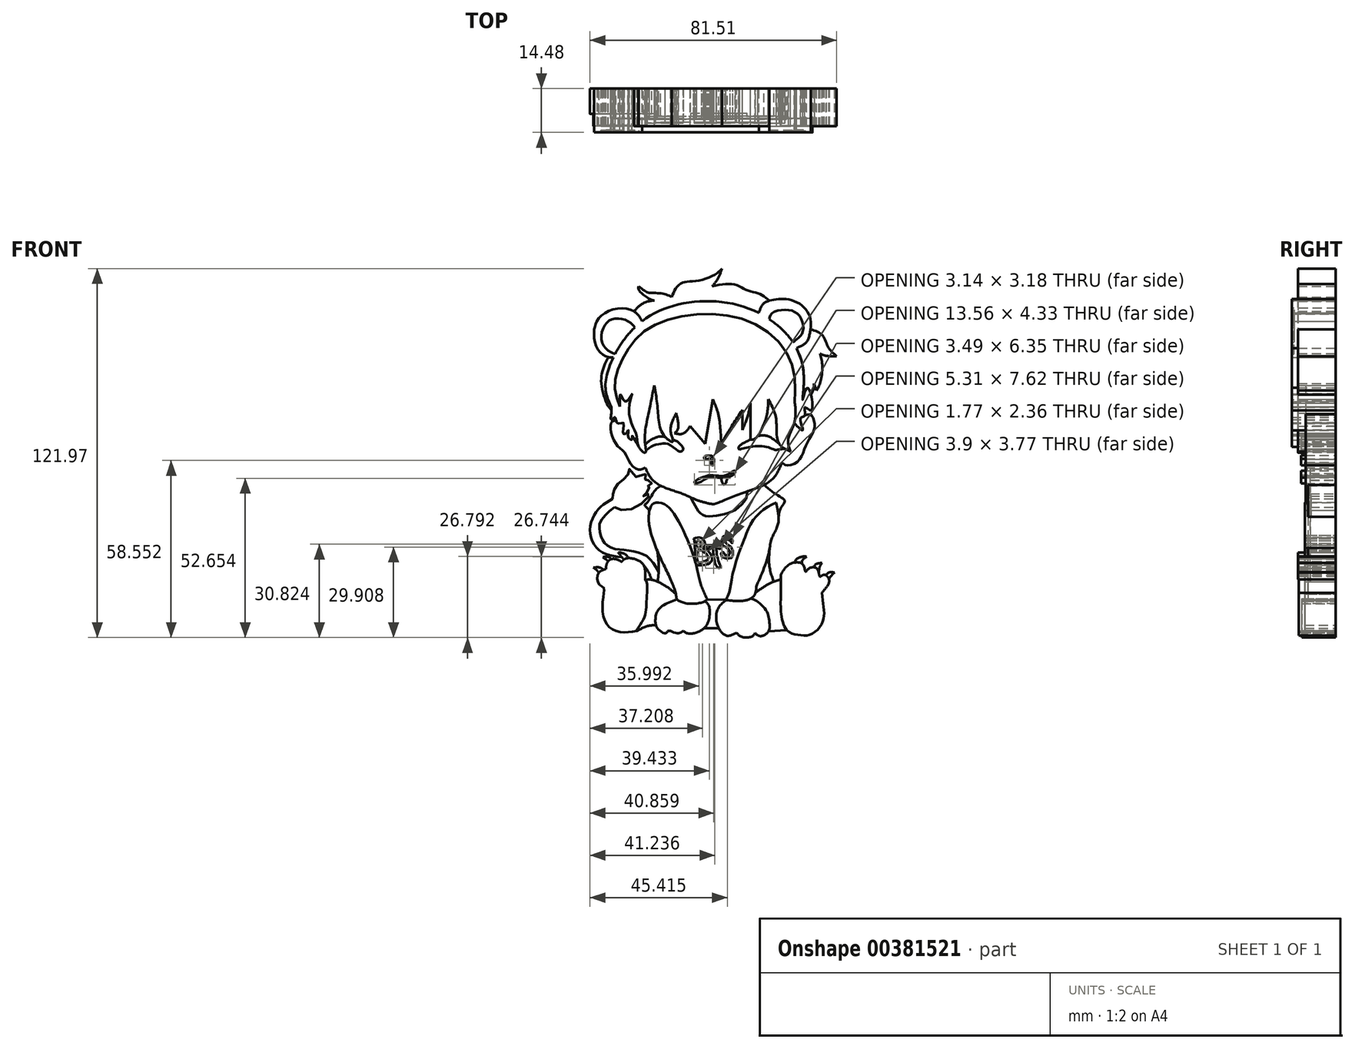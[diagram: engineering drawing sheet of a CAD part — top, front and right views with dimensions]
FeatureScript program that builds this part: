
annotation { "Feature Type Name" : "Feature", "Feature Type Description" : "" }
export const myFeature = defineFeature(function(context is Context, id is Id, definition is map)
    precondition{}
    {
        {
            var Q0;
            Q0=qCreatedBy(makeId("Front.planeOp"),FACE);
            var sketch = newSketch(context, id + "F0", { "sketchPlane" : qUnion([Q0])});
            skFitSpline(sketch, "E0", {"points": [v(-18.55, 26.42) * mm, v(-20.5, 16.98) * mm, v(-21.65, 7.93) * mm, v(-21.53, 4.18) * mm, v(-23.72, 6.12) * mm, v(-24.37, 9.74) * mm, v(-25.8, 13.23) * mm, v(-26.83, 19.7) * mm, v(-25.92, 23.57) * mm, v(-27.99, 21.11) * mm, v(-29.67, 23.31) * mm, v(-29.93, 19.43) * mm], "startDerivative": vector(-14.4, -71.56) * mm, "endDerivative": vector(1.85, -74.93) * mm});
            skFitSpline(sketch, "E1", {"points": [v(-18.55, 26.42) * mm, v(-17.39, 18.27) * mm, v(-15.7, 10.38) * mm, v(-12.48, 7.8) * mm, v(-13.12, 11.29) * mm, v(-11.31, 17.24) * mm], "startDerivative": vector(5.92, -33.92) * mm, "endDerivative": vector(14.7, 28.25) * mm});
            skFitSpline(sketch, "E2", {"points": [v(-11.83, 10.64) * mm, v(-10.67, 12.2) * mm, v(-11.31, 17.24) * mm], "startDerivative": vector(3.83, 3.28) * mm, "endDerivative": vector(-2.31, 9.42) * mm});
            skFitSpline(sketch, "E3", {"points": [v(-11.83, 10.64) * mm, v(-8.73, 10.64) * mm, v(-5.24, 16.98) * mm, v(-5.5, 23.18) * mm], "startDerivative": vector(12.38, -3.46) * mm, "endDerivative": vector(-3, 16.24) * mm});
            skFitSpline(sketch, "E4", {"points": [v(-6.7, 13) * mm, v(-1.74, 7.07) * mm], "startDerivative": vector(4.96, -5.94) * mm, "endDerivative": vector(4.96, -5.94) * mm});
            skFitSpline(sketch, "E5", {"points": [v(0.8, 21.84) * mm, v(-1.74, 7.07) * mm], "startDerivative": vector(-2.54, -14.77) * mm, "endDerivative": vector(-2.54, -14.77) * mm});
            skFitSpline(sketch, "E6", {"points": [v(0.8, 21.84) * mm, v(2.73, 16.3) * mm, v(3.57, 7.07) * mm], "startDerivative": vector(4.99, -11.59) * mm, "endDerivative": vector(0.71, -17.72) * mm});
            skFitSpline(sketch, "E7", {"points": [v(10.53, 18.24) * mm, v(5.58, 10.6) * mm, v(3.57, 7.07) * mm], "startDerivative": vector(-9.23, -13.9) * mm, "endDerivative": vector(-4.37, -8.05) * mm});
            skFitSpline(sketch, "E8", {"points": [v(10.53, 18.24) * mm, v(10.53, 11.7) * mm], "startDerivative": vector(0, -6.54) * mm, "endDerivative": vector(0, -6.54) * mm});
            skFitSpline(sketch, "E9", {"points": [v(13.21, 20.58) * mm, v(12.37, 16.4) * mm, v(10.53, 11.7) * mm], "startDerivative": vector(-1.32, -8.68) * mm, "endDerivative": vector(-4, -9.09) * mm});
            skFitSpline(sketch, "E10", {"points": [v(13.21, 20.58) * mm, v(13.21, 8.51) * mm], "startDerivative": vector(0, -12.07) * mm, "endDerivative": vector(0, -12.07) * mm});
            skFitSpline(sketch, "E11", {"points": [v(19.08, 21.84) * mm, v(18.4, 15.64) * mm, v(14.8, 8.85) * mm, v(13.21, 8.51) * mm], "startDerivative": vector(0.03, -15.04) * mm, "endDerivative": vector(-7.8, 0.75) * mm});
            skFitSpline(sketch, "E12", {"points": [v(19.08, 21.84) * mm, v(21.5, 16.56) * mm, v(21.85, 11.7) * mm, v(22.77, 7.07) * mm, v(26.46, 4.57) * mm], "startDerivative": vector(11.06, -19.58) * mm, "endDerivative": vector(18.37, -8.35) * mm});
            skFitSpline(sketch, "E13", {"points": [v(24.28, 31.23) * mm, v(27.46, 22.85) * mm, v(27.71, 13.96) * mm, v(25.7, 8.51) * mm, v(26.46, 4.57) * mm], "startDerivative": vector(12.77, -28.04) * mm, "endDerivative": vector(7.38, -20.16) * mm});
            skFitSpline(sketch, "E14", {"points": [v(-29.93, 19.43) * mm, v(-31.64, 26.54) * mm, v(-28.7, 35.92) * mm, v(-20.76, 45.07) * mm, v(-4.33, 49.9) * mm, v(14.79, 46.68) * mm, v(26.46, 34.71) * mm, v(27.9, 20.58) * mm], "startDerivative": vector(-24.7, 65.1) * mm, "endDerivative": vector(-3.9, -98.8) * mm});
            skFitSpline(sketch, "E15", {"points": [v(-32.73, 19.2) * mm, v(-34.7, 26.32) * mm, v(-30.8, 38.1) * mm, v(-21.48, 48.47) * mm, v(-7.19, 53.83) * mm, v(10.53, 52.58) * mm, v(24.97, 43.64) * mm, v(30.87, 29.71) * mm, v(30.5, 21.71) * mm, v(32.12, 25.6) * mm, v(33.37, 18.27) * mm, v(31.22, 19.2) * mm, v(31.22, 16.49) * mm, v(29.8, 15.6) * mm, v(30.5, 11.7) * mm, v(27.71, 13.96) * mm], "startDerivative": vector(-45.63, 102.3) * mm, "endDerivative": vector(-89.01, 91.48) * mm});
            skFitSpline(sketch, "E16", {"points": [v(-32.73, 19.2) * mm, v(-32.73, 17.51) * mm, v(-32.73, 15.07) * mm, v(-31.52, 15.86) * mm, v(-30.8, 13.96) * mm, v(-28.74, 13.96) * mm, v(-28.83, 10.55) * mm, v(-27.87, 10.55) * mm, v(-27.09, 11.7) * mm, v(-27.09, 9.24) * mm, v(-25.92, 8.51) * mm, v(-25.92, 9.77) * mm, v(-23.72, 6.12) * mm], "startDerivative": vector(1.52, -17.26) * mm, "endDerivative": vector(25.91, -48.27) * mm});
            skFitSpline(sketch, "E17", {"points": [v(-33.7, 35.78) * mm, v(-35.74, 31) * mm, v(-35.8, 25.32) * mm, v(-33.7, 19.43) * mm, v(-32.69, 18.31) * mm], "startDerivative": vector(-8.88, -17.25) * mm, "endDerivative": vector(6.63, -5.51) * mm});
            skFitSpline(sketch, "E18", {"points": [v(-32.11, 35.62) * mm, v(-33.7, 35.78) * mm, v(-36.86, 37.78) * mm, v(-38.46, 42.85) * mm, v(-38.26, 45.49) * mm, v(-36.8, 48.78) * mm, v(-30.8, 51.81) * mm, v(-24.86, 50.62) * mm, v(-22.6, 47.65) * mm], "startDerivative": vector(-18.4, 0.14) * mm, "endDerivative": vector(14.36, -27.23) * mm});
            skFitSpline(sketch, "E19", {"points": [v(-31.5, 36.82) * mm, v(-33.7, 37.9) * mm, v(-35.98, 41.05) * mm, v(-35.2, 45.75) * mm, v(-32.73, 48.24) * mm, v(-28.6, 48.24) * mm, v(-25.92, 46.76) * mm, v(-25.03, 45.56) * mm], "startDerivative": vector(-17.52, 6.5) * mm, "endDerivative": vector(7.45, -12.42) * mm});
            skFitSpline(sketch, "E20", {"points": [v(-15.84, 53.96) * mm, v(-19.35, 54.42) * mm, v(-22.95, 53.12) * mm, v(-25.25, 50.87) * mm], "startDerivative": vector(-10.34, 2.5) * mm, "endDerivative": vector(-6.42, -7.57) * mm});
            skFitSpline(sketch, "E21", {"points": [v(-12.74, 55.63) * mm, v(-15.75, 56.76) * mm, v(-19.48, 56.97) * mm, v(-20.9, 57.22) * mm, v(-23.72, 59.15) * mm], "startDerivative": vector(-10.48, 5.16) * mm, "endDerivative": vector(-11.44, 8.74) * mm});
            skFitSpline(sketch, "E22", {"points": [v(-18.55, 54.43) * mm, v(-20.44, 55.21) * mm, v(-23.72, 58.1) * mm, v(-23.72, 59.15) * mm], "startDerivative": vector(-5.2, 1.51) * mm, "endDerivative": vector(1.36, 4.15) * mm});
            skFitSpline(sketch, "E23", {"points": [v(-12.74, 55.63) * mm, v(-11.44, 58.43) * mm, v(-9.02, 60.44) * mm, v(-5.13, 60.9) * mm, v(1.2, 62.89) * mm, v(3.8, 65.04) * mm], "startDerivative": vector(6, 16.35) * mm, "endDerivative": vector(11.38, 12.05) * mm});
            skFitSpline(sketch, "E24", {"points": [v(0.6, 59.21) * mm, v(2.46, 61.66) * mm, v(3.8, 65.04) * mm], "startDerivative": vector(4.2, 4.78) * mm, "endDerivative": vector(2.23, 6.85) * mm});
            skFitSpline(sketch, "E25", {"points": [v(0.6, 59.21) * mm, v(7.96, 59.8) * mm, v(12.2, 57.9) * mm, v(16.43, 56.62) * mm, v(19.45, 54.42) * mm], "startDerivative": vector(26.23, 5.07) * mm, "endDerivative": vector(12.76, -11.67) * mm});
            skFitSpline(sketch, "E26", {"points": [v(19.45, 54.42) * mm, v(17.44, 53.37) * mm, v(16, 50.35) * mm], "startDerivative": vector(-4.85, -1.6) * mm, "endDerivative": vector(-2.17, -6.41) * mm});
            skFitSpline(sketch, "E27", {"points": [v(19.45, 54.42) * mm, v(23.82, 55.04) * mm, v(29.49, 53.41) * mm, v(32.98, 48.8) * mm, v(32.92, 43.94) * mm, v(31.6, 40.57) * mm, v(28.44, 38.77) * mm], "startDerivative": vector(25.67, 5.92) * mm, "endDerivative": vector(-24.61, -9.76) * mm});
            skFitSpline(sketch, "E28", {"points": [v(19.45, 48.33) * mm, v(20.32, 50.23) * mm, v(25.25, 51.42) * mm, v(29.3, 49.55) * mm, v(30.74, 45.18) * mm, v(29.3, 42.25) * mm, v(27.21, 40.81) * mm], "startDerivative": vector(3.02, 16.1) * mm, "endDerivative": vector(-15.56, -8.68) * mm});
            skFitSpline(sketch, "E29", {"points": [v(33.09, 44.93) * mm, v(36.97, 43.06) * mm, v(38.97, 39.01) * mm, v(41.7, 36.08) * mm], "startDerivative": vector(13.33, -3.73) * mm, "endDerivative": vector(9.57, -7.95) * mm});
            skFitSpline(sketch, "E30", {"points": [v(36.29, 36.95) * mm, v(37.97, 36.27) * mm, v(41.7, 36.08) * mm], "startDerivative": vector(3.64, -1.95) * mm, "endDerivative": vector(7, 0.08) * mm});
            skFitSpline(sketch, "E31", {"points": [v(36.29, 36.95) * mm, v(36.97, 32.9) * mm, v(36.29, 27.3) * mm, v(35.16, 24.8) * mm], "startDerivative": vector(2.82, -11.18) * mm, "endDerivative": vector(-4.41, -7.86) * mm});
            skFitSpline(sketch, "E32", {"points": [v(34.23, 27.1) * mm, v(35.16, 24.8) * mm], "startDerivative": vector(0.94, -2.3) * mm, "endDerivative": vector(0.94, -2.3) * mm});
            skFitSpline(sketch, "E33", {"points": [v(34.23, 27.1) * mm, v(34.04, 25) * mm, v(33.25, 23.33) * mm], "startDerivative": vector(-0.03, -4.23) * mm, "endDerivative": vector(-1.96, -3.32) * mm});
            skFitSpline(sketch, "E34", {"points": [v(-21.53, -0.78) * mm, v(-23.65, -1.43) * mm, v(-26.44, 0.62) * mm, v(-28.34, 4.18) * mm, v(-30.99, 6.79) * mm, v(-32.97, 11.7) * mm, v(-32.6, 14.35) * mm, v(-31.2, 14.93) * mm], "startDerivative": vector(-16.97, -9.49) * mm, "endDerivative": vector(16.15, 3.19) * mm});
            skFitSpline(sketch, "E35", {"points": [v(-22.2, 0.3) * mm, v(-21.53, -0.78) * mm, v(-18.65, -5.3) * mm, v(-9.77, -9.2) * mm, v(-4.64, -11.42) * mm, v(0, -12.73) * mm], "startDerivative": vector(6.28, -8.26) * mm, "endDerivative": vector(24.05, -5.75) * mm});
            skFitSpline(sketch, "E36", {"points": [v(0, -12.73) * mm, v(1.5, -12.73) * mm, v(5.45, -11.11) * mm, v(13.44, -8.2) * mm, v(20.57, -4.5) * mm, v(23.66, 0.97) * mm], "startDerivative": vector(13, -1.7) * mm, "endDerivative": vector(11.23, 27.55) * mm});
            skFitSpline(sketch, "E37", {"points": [v(23.66, 0.97) * mm, v(25, 0) * mm, v(28.48, 0.97) * mm, v(30.62, 4.18) * mm, v(32.6, 8.64) * mm, v(34.23, 11.65) * mm, v(34.23, 14.91) * mm, v(33.12, 16.8) * mm, v(31.22, 16.49) * mm], "startDerivative": vector(12.26, -13.1) * mm, "endDerivative": vector(-20.68, -7.96) * mm});
            skFitSpline(sketch, "E38", {"points": [v(9.66, 5.22) * mm, v(13.27, 6.12) * mm, v(18.51, 6.12) * mm, v(21.73, 5.1) * mm, v(23.66, 5.3) * mm], "startDerivative": vector(12.97, 4) * mm, "endDerivative": vector(12.7, -2.3) * mm});
            skFitSpline(sketch, "E39", {"points": [v(9.66, 5.22) * mm, v(9.28, 5.6) * mm, v(9.66, 6.43) * mm, v(13.21, 8.51) * mm], "startDerivative": vector(-2.54, 1.7) * mm, "endDerivative": vector(7.96, 3.9) * mm});
            skFitSpline(sketch, "E40", {"points": [v(15.65, 9.74) * mm, v(18.76, 9.74) * mm, v(22.77, 7.07) * mm], "startDerivative": vector(6.92, 1.07) * mm, "endDerivative": vector(7.3, -6.15) * mm});
            skFitSpline(sketch, "E41", {"points": [v(-20.97, 5.22) * mm, v(-18.5, 6.63) * mm, v(-16.24, 7.07) * mm, v(-13.94, 7.07) * mm, v(-10.74, 4.78) * mm, v(-9.76, 4.57) * mm, v(-9.01, 5.22) * mm, v(-9.98, 7.07) * mm, v(-12.5, 8.7) * mm], "startDerivative": vector(16.81, 12.03) * mm, "endDerivative": vector(-18.51, 9.4) * mm});
            skFitSpline(sketch, "E42", {"points": [v(-14.96, 9.41) * mm, v(-16.17, 9.54) * mm, v(-17.82, 9.3) * mm, v(-20.17, 8.1) * mm, v(-21.54, 6.84) * mm], "startDerivative": vector(-5.79, 0.89) * mm, "endDerivative": vector(-4.67, -5.03) * mm});
            skFitSpline(sketch, "E43", {"points": [v(-1.94, 2.81) * mm, v(0.8, 2.81) * mm, v(0.8, 0) * mm, v(0.3, 0.5) * mm, v(0.4, 1.58) * mm, v(0.28, 2.07) * mm, v(-0.32, 2.16) * mm, v(-1.16, 2.06) * mm, v(-1.74, 2.13) * mm, v(-2.04, 2.2) * mm, v(-1.94, 2.81) * mm]});
            skFitSpline(sketch, "E44", {"points": [v(-5.38, -5.64) * mm, v(-2.06, -3.76) * mm, v(0.94, -3.32) * mm, v(4.95, -3.34) * mm, v(7.63, -1.9) * mm, v(8.1, -1.83) * mm, v(8.12, -2.54) * mm, v(5.68, -3.9) * mm, v(3.31, -4.03) * mm, v(0.65, -4.08) * mm, v(-1.5, -4.42) * mm, v(-4.23, -5.88) * mm, v(-5.38, -5.64) * mm]});
            skFitSpline(sketch, "E45", {"points": [v(3.6, -4.04) * mm, v(3.8, -5.37) * mm, v(4.53, -6.45) * mm, v(5.36, -5.05) * mm, v(5.68, -3.9) * mm], "startDerivative": vector(0.23, -4.92) * mm, "endDerivative": vector(0.97, 4.2) * mm});
            skFitSpline(sketch, "E46", {"points": [v(-20.17, -14.87) * mm, v(-18.97, -12.73) * mm, v(-15.35, -12.73) * mm, v(-10.13, -19.2) * mm, v(-4.86, -32.28) * mm, v(-3.11, -39.48) * mm, v(-1, -44.31) * mm], "startDerivative": vector(7.43, 24.09) * mm, "endDerivative": vector(15.57, -30.67) * mm});
            skFitSpline(sketch, "E47", {"points": [v(-1, -44.31) * mm, v(-2.82, -45.35) * mm, v(-8.44, -45.54) * mm, v(-11.15, -44.31) * mm], "startDerivative": vector(-5.43, -4.42) * mm, "endDerivative": vector(-7.24, 4.73) * mm});
            skFitSpline(sketch, "E48", {"points": [v(-1.84, -44.93) * mm, v(-0.5, -46.53) * mm, v(-1, -52.33) * mm, v(-4.2, -55.13) * mm, v(-7.64, -55.53) * mm, v(-9.4, -54.13) * mm], "startDerivative": vector(10.15, -7.4) * mm, "endDerivative": vector(-9.3, 10.8) * mm});
            skFitSpline(sketch, "E49", {"points": [v(-8.9, -54.71) * mm, v(-11.14, -55.53) * mm, v(-13.94, -54.71) * mm, v(-14.7, -55.53) * mm, v(-17.4, -54.03) * mm, v(-18.2, -51.23) * mm, v(-17.04, -47.53) * mm, v(-11.15, -44.31) * mm], "startDerivative": vector(-16.16, -11.36) * mm, "endDerivative": vector(33.64, 12.73) * mm});
            skFitSpline(sketch, "E50", {"points": [v(-11.15, -44.31) * mm, v(-12, -40.47) * mm, v(-15.9, -31.94) * mm, v(-20.17, -20.22) * mm, v(-20.17, -14.87) * mm], "startDerivative": vector(-2.92, 19.6) * mm, "endDerivative": vector(2.63, 22.62) * mm});
            skFitSpline(sketch, "E51", {"points": [v(-17.5, -28.36) * mm, v(-17.07, -33.89) * mm, v(-17.43, -38.45) * mm], "startDerivative": vector(1.25, -10.8) * mm, "endDerivative": vector(-1.14, -9.35) * mm});
            skFitSpline(sketch, "E52", {"points": [v(-17.43, -38.45) * mm, v(-13.94, -40.47) * mm, v(-11.45, -42.53) * mm], "startDerivative": vector(6.95, -3.7) * mm, "endDerivative": vector(4.98, -4.46) * mm});
            skFitSpline(sketch, "E53", {"points": [v(-17.43, -38.45) * mm, v(-19.45, -37.83) * mm, v(-20.72, -37.78) * mm], "startDerivative": vector(-3.78, 1.39) * mm, "endDerivative": vector(-2.77, -0.12) * mm});
            skFitSpline(sketch, "E54", {"points": [v(-18.03, -52.85) * mm, v(-21.87, -53.5) * mm, v(-24.37, -54.71) * mm, v(-22.2, -50.99) * mm, v(-21.1, -44.8) * mm, v(-21.15, -38.45) * mm, v(-21.53, -37.91) * mm, v(-20.72, -37.78) * mm], "startDerivative": vector(-23.55, -0.55) * mm, "endDerivative": vector(15.9, 0.86) * mm});
            skFitSpline(sketch, "E55", {"points": [v(-21.53, -37.91) * mm, v(-21.53, -35.7) * mm, v(-22.2, -32.77) * mm, v(-24.92, -31.03) * mm, v(-27.81, -30.78) * mm, v(-29.3, -31.92) * mm, v(-29.72, -33.4) * mm], "startDerivative": vector(0.27, 13.05) * mm, "endDerivative": vector(-1.76, -11.54) * mm});
            skFitSpline(sketch, "E56", {"points": [v(-29.3, -31.92) * mm, v(-30.66, -31.2) * mm, v(-33.16, -31.16) * mm, v(-34.48, -33.58) * mm, v(-34.05, -35.53) * mm], "startDerivative": vector(-5.6, 3.66) * mm, "endDerivative": vector(3, -7.5) * mm});
            skFitSpline(sketch, "E57", {"points": [v(-34.45, -34.25) * mm, v(-36.22, -34.93) * mm, v(-37.24, -36.13) * mm, v(-36.86, -39.27) * mm, v(-35.29, -40.46) * mm, v(-35.29, -42.75) * mm, v(-35.54, -49.16) * mm, v(-33.42, -53.5) * mm, v(-29.3, -55.15) * mm, v(-24.37, -54.71) * mm], "startDerivative": vector(-22.52, -7.15) * mm, "endDerivative": vector(36.62, 6.5) * mm});
            skFitSpline(sketch, "E58", {"points": [v(-36.95, -35.53) * mm, v(-37.43, -34.79) * mm, v(-38.65, -33.79) * mm], "startDerivative": vector(-0.9, 1.74) * mm, "endDerivative": vector(-2.44, 1.75) * mm});
            skFitSpline(sketch, "E59", {"points": [v(-35.46, -34.6) * mm, v(-36.33, -33.86) * mm, v(-38.65, -33.79) * mm], "startDerivative": vector(-1.74, 2.13) * mm, "endDerivative": vector(-4.5, -0.37) * mm});
            skFitSpline(sketch, "E60", {"points": [v(-32.82, -31.01) * mm, v(-33.23, -30.52) * mm, v(-34.48, -30.2) * mm, v(-35.54, -30.34) * mm], "startDerivative": vector(-1.12, 1.97) * mm, "endDerivative": vector(-2.84, -0.68) * mm});
            skFitSpline(sketch, "E61", {"points": [v(-33.84, -31.79) * mm, v(-34.3, -31.26) * mm, v(-35.12, -30.73) * mm, v(-35.54, -30.34) * mm], "startDerivative": vector(-1.17, 1.7) * mm, "endDerivative": vector(-1.2, 1.35) * mm});
            skFitSpline(sketch, "E62", {"points": [v(-27.11, -30.67) * mm, v(-28.11, -29.42) * mm, v(-30, -28.83) * mm, v(-30.46, -28.86) * mm], "startDerivative": vector(-1.98, 3.63) * mm, "endDerivative": vector(-1.77, -0.37) * mm});
            skFitSpline(sketch, "E63", {"points": [v(-28.6, -31.16) * mm, v(-29.3, -30.34) * mm, v(-30.46, -28.86) * mm], "startDerivative": vector(-1.53, 1.76) * mm, "endDerivative": vector(-2.17, 2.79) * mm});
            skFitSpline(sketch, "E64", {"points": [v(-17.1, -35.2) * mm, v(-20.17, -30.78) * mm, v(-23.72, -28.86) * mm, v(-28.45, -27.99) * mm, v(-32.49, -27.36) * mm, v(-35.2, -25.35) * mm, v(-36.41, -22.56) * mm, v(-36.41, -18.76) * mm, v(-31.67, -13.8) * mm], "startDerivative": vector(-20.27, 35.87) * mm, "endDerivative": vector(38.72, 30.91) * mm});
            skFitSpline(sketch, "E65", {"points": [v(-19.45, -37.83) * mm, v(-20.32, -35.53) * mm, v(-22.2, -32.77) * mm], "startDerivative": vector(-1.52, 4.93) * mm, "endDerivative": vector(-3.93, 5.17) * mm});
            skFitSpline(sketch, "E66", {"points": [v(-32.4, -11.11) * mm, v(-36.52, -13.94) * mm, v(-39.35, -18.62) * mm, v(-39.35, -24.34) * mm, v(-35.54, -28.86) * mm, v(-29.3, -30.34) * mm], "startDerivative": vector(-23.27, -13.18) * mm, "endDerivative": vector(31.19, -3.31) * mm});
            skFitSpline(sketch, "E67", {"points": [v(-26.65, -1.16) * mm, v(-27.15, -2.86) * mm, v(-30.46, -6) * mm, v(-32.1, -8.8) * mm, v(-32.4, -11.11) * mm, v(-31.67, -13.8) * mm, v(-24.37, -13.8) * mm, v(-20.32, -9.47) * mm, v(-22.2, -10.21) * mm, v(-20.17, -7.82) * mm, v(-20.72, -6.82) * mm, v(-19.45, -6.16) * mm, v(-20.72, -4.92) * mm, v(-21.53, -4.76) * mm, v(-21.53, -2.7) * mm, v(-24.37, -3.9) * mm, v(-26.65, -1.16) * mm]});
            skFitSpline(sketch, "E68", {"points": [v(-6.49, -10.62) * mm, v(-4.75, -13.8) * mm, v(-2.44, -16.5) * mm, v(2.19, -16.57) * mm, v(7.97, -14.87) * mm, v(11.69, -11.11) * mm, v(12.16, -8.65) * mm], "startDerivative": vector(10.75, -20.38) * mm, "endDerivative": vector(0.6, 18.24) * mm});
            skFitSpline(sketch, "E69", {"points": [v(21.73, -12.3) * mm, v(22.36, -15.55) * mm, v(22.36, -19.43) * mm, v(20.07, -24.75) * mm, v(19.43, -28.5) * mm, v(16.07, -38) * mm, v(15.25, -39.94) * mm, v(14.64, -42.79) * mm, v(11.29, -44.72) * mm, v(5.18, -44.52) * mm], "startDerivative": vector(7.06, -33.3) * mm, "endDerivative": vector(-48.82, 6.12) * mm});
            skFitSpline(sketch, "E70", {"points": [v(21.73, -12.3) * mm, v(17.24, -14.93) * mm, v(13.5, -19.18) * mm, v(11.41, -23.78) * mm, v(10.62, -25.82) * mm, v(7.41, -35.62) * mm, v(6.55, -40.8) * mm, v(5.18, -44.52) * mm], "startDerivative": vector(-32.36, -16.31) * mm, "endDerivative": vector(-12.87, -29.45) * mm});
            skFitSpline(sketch, "E71", {"points": [v(14.94, -42.03) * mm, v(20, -38.85) * mm, v(23.17, -37.77) * mm], "startDerivative": vector(9.3, 6.4) * mm, "endDerivative": vector(7.09, 1.88) * mm});
            skFitSpline(sketch, "E72", {"points": [v(19.86, -25.58) * mm, v(19.69, -26.86) * mm, v(19.43, -32.74) * mm, v(20.97, -38.44) * mm], "startDerivative": vector(-0.8, -5.34) * mm, "endDerivative": vector(4.98, -13.2) * mm});
            skFitSpline(sketch, "E73", {"points": [v(5.18, -44.52) * mm, v(2.37, -47.7) * mm, v(2.37, -52.88) * mm, v(5.18, -56.27) * mm, v(8.7, -55.4) * mm], "startDerivative": vector(-13.55, -11.26) * mm, "endDerivative": vector(15.98, 7.7) * mm});
            skFitSpline(sketch, "E74", {"points": [v(8.7, -55.4) * mm, v(10.5, -56.77) * mm, v(13.92, -56.48) * mm, v(14.75, -55.4) * mm], "startDerivative": vector(4.3, -5.03) * mm, "endDerivative": vector(1.97, 4.63) * mm});
            skFitSpline(sketch, "E75", {"points": [v(14.75, -55.4) * mm, v(16.55, -56.48) * mm, v(19.21, -54.83) * mm, v(19.43, -51.37) * mm, v(18.42, -47.92) * mm, v(14.75, -44.52) * mm, v(13.26, -44.07) * mm], "startDerivative": vector(11.47, -11.44) * mm, "endDerivative": vector(-10.98, 1.57) * mm});
            skFitSpline(sketch, "E76", {"points": [v(-5.56, -24.26) * mm, v(-5.35, -24.71) * mm, v(-5.1, -27.38) * mm, v(-4.86, -32.28) * mm], "startDerivative": vector(1.47, -2.28) * mm, "endDerivative": vector(0.52, -10.42) * mm});
            skFitSpline(sketch, "E77", {"points": [v(-5.56, -24.26) * mm, v(-3.9, -23.84) * mm, v(-2.2, -24.62) * mm, v(-1.9, -26.77) * mm, v(-2.38, -27.5) * mm, v(-1.08, -28.04) * mm, v(0.58, -30.46) * mm, v(0.31, -31.73) * mm, v(-1.38, -32.85) * mm, v(-4.65, -33.06) * mm], "startDerivative": vector(15.22, 6) * mm, "endDerivative": vector(-23.92, 0.84) * mm});
            skFitSpline(sketch, "E78", {"points": [v(-4.4, -24.92) * mm, v(-4.32, -27.16) * mm, v(-3.23, -26.86) * mm, v(-3.02, -25.65) * mm, v(-4.4, -24.92) * mm]});
            skFitSpline(sketch, "E79", {"points": [v(-4.04, -28.25) * mm, v(-4.01, -31.97) * mm, v(-2.32, -31.8) * mm, v(-0.72, -30.98) * mm, v(-1.23, -29.37) * mm, v(-4.04, -28.25) * mm]});
            skFitSpline(sketch, "E80", {"points": [v(-1.5, -26.44) * mm, v(1.46, -26.38) * mm, v(3.3, -26.38) * mm], "startDerivative": vector(5.62, 0.14) * mm, "endDerivative": vector(3.94, -0.02) * mm});
            skFitSpline(sketch, "E81", {"points": [v(-1.5, -26.44) * mm, v(-1.5, -27.22) * mm, v(0.98, -27.2) * mm], "startDerivative": vector(-0.7, -2.59) * mm, "endDerivative": vector(5.12, 0.76) * mm});
            skFitSpline(sketch, "E82", {"points": [v(3.3, -26.38) * mm, v(3.73, -26.95) * mm, v(3.3, -27.56) * mm, v(1.95, -27.2) * mm], "startDerivative": vector(2.1, -1.79) * mm, "endDerivative": vector(-3.67, 1.78) * mm});
            skFitSpline(sketch, "E83", {"points": [v(0.98, -27.2) * mm, v(0.98, -28.7) * mm, v(1.28, -31.19) * mm, v(1.98, -33.27) * mm, v(2.94, -34) * mm, v(3.3, -33.55) * mm, v(2.82, -31.97) * mm, v(2.16, -29.67) * mm, v(1.95, -27.2) * mm], "startDerivative": vector(-0.39, -12.11) * mm, "endDerivative": vector(-0.73, 16.74) * mm});
            skFitSpline(sketch, "E84", {"points": [v(4.88, -29.58) * mm, v(4.34, -28.8) * mm, v(3.76, -28.65) * mm, v(3.49, -29.43) * mm, v(4.58, -30.73) * mm, v(6.4, -30.8) * mm, v(7.24, -30.34) * mm, v(7.42, -29.52) * mm, v(7.24, -27.5) * mm, v(6.09, -26.44) * mm, v(4.9, -25.53) * mm, v(4.88, -24.74) * mm, v(5.58, -24.14) * mm, v(6.63, -25.08) * mm, v(7.2, -25.74) * mm, v(7.45, -25.1) * mm, v(6.82, -23.84) * mm, v(6.12, -23.23) * mm, v(4.6, -23.23) * mm, v(3.88, -24.53) * mm, v(4, -26.38) * mm, v(5.94, -27.56) * mm, v(6.48, -29.22) * mm, v(6, -29.83) * mm, v(4.88, -29.58) * mm]});
            skFitSpline(sketch, "E85", {"points": [v(-20.17, -14.87) * mm, v(-21.7, -13.09) * mm, v(-21.03, -12.48) * mm, v(-18.54, -8.6) * mm, v(-16.41, -6.75) * mm], "startDerivative": vector(-9.52, 8.87) * mm, "endDerivative": vector(8.07, 5.28) * mm});
            skFitSpline(sketch, "E86", {"points": [v(17.65, -6.49) * mm, v(22.83, -10.29) * mm, v(24.56, -11.76) * mm, v(23.18, -14.3) * mm, v(22.56, -17.06) * mm], "startDerivative": vector(16.09, -12.71) * mm, "endDerivative": vector(-0.92, -12.1) * mm});
            skLineSegment(sketch, "E87", {"start": v(-1, -44.31) * mm, "end": v(5.18, -44.52) * mm});
            skLineSegment(sketch, "E88", {"start": v(-2.05, -53.82) * mm, "end": v(0, -53.82) * mm});
            skLineSegment(sketch, "E89", {"start": v(0, -53.82) * mm, "end": v(2.76, -53.82) * mm});
            skLineSegment(sketch, "E90", {"start": v(19.21, -54.83) * mm, "end": v(25.25, -54.47) * mm});
            skLineSegment(sketch, "E91", {"start": v(23.17, -37.77) * mm, "end": v(23.3, -37.77) * mm});
            skLineSegment(sketch, "E92", {"start": v(-8.9, -54.71) * mm, "end": v(-8.87, -54.71) * mm});
            skFitSpline(sketch, "E93", {"points": [v(23.3, -37.77) * mm, v(23.3, -36.4) * mm, v(24.32, -34.46) * mm, v(26.76, -32.42) * mm, v(30.63, -32.83) * mm, v(31.44, -35.17) * mm, v(32.36, -34.25) * mm, v(35.2, -34.15) * mm, v(36.22, -36.8) * mm, v(37.44, -36.19) * mm, v(39.27, -38.04) * mm, v(37.65, -41.17) * mm, v(36.83, -42.2) * mm], "startDerivative": vector(-2.56, 20.98) * mm, "endDerivative": vector(-10.3, -13.54) * mm});
            skFitSpline(sketch, "E94", {"points": [v(23.3, -37.77) * mm, v(23.3, -42.2) * mm, v(23.3, -48) * mm, v(25.25, -54.47) * mm, v(29.4, -56.13) * mm, v(33.58, -55.72) * mm, v(37.04, -51.96) * mm, v(37.54, -48) * mm, v(36.83, -42.2) * mm], "startDerivative": vector(0.48, -36.97) * mm, "endDerivative": vector(-6.64, 45.3) * mm});
            skFitSpline(sketch, "E95", {"points": [v(27.99, -32.11) * mm, v(28.5, -31.01) * mm, v(30.87, -30.11) * mm, v(31.77, -30.22) * mm], "startDerivative": vector(0.69, 3.84) * mm, "endDerivative": vector(2.8, -0.83) * mm});
            skFitSpline(sketch, "E96", {"points": [v(30.32, -32.54) * mm, v(30.3, -31.62) * mm, v(31.77, -30.22) * mm], "startDerivative": vector(-0.57, 2.27) * mm, "endDerivative": vector(3.22, 2.36) * mm});
            skFitSpline(sketch, "E97", {"points": [v(34.46, -33.73) * mm, v(34.68, -32.83) * mm, v(36.88, -32.23) * mm], "startDerivative": vector(-0.02, 2.57) * mm, "endDerivative": vector(4.52, 0.57) * mm});
            skFitSpline(sketch, "E98", {"points": [v(35.83, -35.69) * mm, v(36.12, -33.6) * mm, v(36.88, -32.23) * mm], "startDerivative": vector(0.24, 4.13) * mm, "endDerivative": vector(1.89, 2.74) * mm});
            skFitSpline(sketch, "E99", {"points": [v(38.29, -36.43) * mm, v(39.03, -35.47) * mm, v(41.01, -35.44) * mm], "startDerivative": vector(1.3, 2.65) * mm, "endDerivative": vector(4.04, -0.53) * mm});
            skFitSpline(sketch, "E100", {"points": [v(39.2, -37.66) * mm, v(39.86, -36.62) * mm, v(41.01, -35.44) * mm], "startDerivative": vector(1.25, 2.25) * mm, "endDerivative": vector(2.34, 2.2) * mm});
            skLineSegment(sketch, "E101", {"start": v(23.47, 0.51) * mm, "end": v(24.04, 0.57) * mm});
            skLineSegment(sketch, "E102", {"start": v(24.04, 0.57) * mm, "end": v(24.04, 0.57) * mm});
            skFitSpline(sketch, "E103", {"points": [v(23.66, 5.3) * mm, v(24.68, 5.44) * mm], "startDerivative": vector(1.02, 0.14) * mm, "endDerivative": vector(1.02, 0.14) * mm});
            skFitSpline(sketch, "E104", {"points": [v(-20.97, 5.22) * mm, v(-21.31, 4.9) * mm], "startDerivative": vector(-0.35, -0.32) * mm, "endDerivative": vector(-0.35, -0.32) * mm});
            skSolve(sketch);
        }
        {
            var Q0;
            {var subQ24=sQuery(id+"F0.wireOp",EDGE,"E2");Q0=makeQuery(id+"F0.imprint","IMPRINT",FACE,{"disambiguationData":[TD([[makeQuery(id+"F0.imprint","IMPRINT",EDGE,{"derivedFrom":subQ24}),-1.0]])]});}
            var Q1;
            Q1=makeQuery(id+"F0.imprint","IMPRINT",FACE,{"disambiguationData":[TD([[makeQuery(id+"F0.imprint","IMPRINT",EDGE,{"derivedFrom":sQuery(id+"F0.wireOp",EDGE,"E21")}),1.0]])]});
            var Q2;
            {var subQ4=sQuery(id+"F0.wireOp",EDGE,"E29");Q2=makeQuery(id+"F0.imprint","IMPRINT",FACE,{"disambiguationData":[TD([[makeQuery(id+"F0.imprint","IMPRINT",EDGE,{"derivedFrom":subQ4}),-1.0]])]});}
            var Q3;
            {var subQ5=sQuery(id+"F0.wireOp",EDGE,"E17");Q3=makeQuery(id+"F0.imprint","IMPRINT",FACE,{"disambiguationData":[TD([[makeQuery(id+"F0.imprint","IMPRINT",EDGE,{"derivedFrom":subQ5}),1.0]])]});}
            extrude(context, id + "F1", {"entities" : qUnion([Q0, Q1, Q2, Q3]), "depth" : 12.45 * mm});
        }
        {
            var Q0;
            {var subQ10=sQuery(id+"F0.wireOp",EDGE,"E14");Q0=makeQuery(id+"F0.imprint","IMPRINT",FACE,{"disambiguationData":[TD([[makeQuery(id+"F0.imprint","IMPRINT",EDGE,{"derivedFrom":subQ10}),1.0]])]});}
            var Q1;
            {var subQ5=sQuery(id+"F0.wireOp",EDGE,"E19");Q1=makeQuery(id+"F0.imprint","IMPRINT",FACE,{"disambiguationData":[TD([[makeQuery(id+"F0.imprint","IMPRINT",EDGE,{"derivedFrom":subQ5}),1.0]])]});}
            var Q2;
            {var subQ1=sQuery(id+"F0.wireOp",EDGE,"E26");Q2=makeQuery(id+"F0.imprint","IMPRINT",FACE,{"disambiguationData":[TD([[makeQuery(id+"F0.imprint","IMPRINT",EDGE,{"derivedFrom":subQ1}),1.0]])]});}
            extrude(context, id + "F2", {"entities" : qUnion([Q0, Q1, Q2]), "depth" : 14.48 * mm});
        }
        {
            var Q0;
            {var subQ18=sQuery(id+"F0.wireOp",EDGE,"E2");Q0=makeQuery(id+"F0.imprint","IMPRINT",FACE,{"disambiguationData":[TD([[makeQuery(id+"F0.imprint","IMPRINT",EDGE,{"derivedFrom":subQ18}),1.0]])]});}
            var Q1;
            {var subQ5=sQuery(id+"F0.wireOp",EDGE,"E37");Q1=makeQuery(id+"F0.imprint","IMPRINT",FACE,{"disambiguationData":[TD([[makeQuery(id+"F0.imprint","IMPRINT",EDGE,{"derivedFrom":subQ5}),1.0]])]});}
            var Q2;
            {var subQ5=sQuery(id+"F0.wireOp",EDGE,"E34");Q2=makeQuery(id+"F0.imprint","IMPRINT",FACE,{"disambiguationData":[TD([[makeQuery(id+"F0.imprint","IMPRINT",EDGE,{"derivedFrom":subQ5}),-1.0]])]});}
            var Q3;
            {var subQ3=sQuery(id+"F0.wireOp",EDGE,"E42");Q3=makeQuery(id+"F0.imprint","IMPRINT",FACE,{"disambiguationData":[TD([[makeQuery(id+"F0.imprint","IMPRINT",EDGE,{"derivedFrom":subQ3}),-1.0]])]});}
            var Q4;
            {var subQ3=sQuery(id+"F0.wireOp",EDGE,"E40");Q4=makeQuery(id+"F0.imprint","IMPRINT",FACE,{"disambiguationData":[TD([[makeQuery(id+"F0.imprint","IMPRINT",EDGE,{"derivedFrom":subQ3}),1.0]])]});}
            extrude(context, id + "F3", {"entities" : qUnion([Q0, Q1, Q2, Q3, Q4]), "depth" : 9.9 * mm});
        }
        {
            var Q0;
            Q0=makeQuery(id+"F0.imprint","IMPRINT",FACE,{"disambiguationData":[TD([[makeQuery(id+"F0.imprint","IMPRINT",EDGE,{"derivedFrom":sQuery(id+"F0.wireOp",EDGE,"E43")}),-1.0]])]});
            var Q1;
            {var subQ7=sQuery(id+"F0.wireOp",EDGE,"E39");Q1=makeQuery(id+"F0.imprint","IMPRINT",FACE,{"disambiguationData":[TD([[makeQuery(id+"F0.imprint","IMPRINT",EDGE,{"derivedFrom":subQ7}),-1.0]])]});}
            var Q2;
            {var subQ0=sQuery(id+"F0.wireOp",EDGE,"E41");Q2=makeQuery(id+"F0.imprint","IMPRINT",FACE,{"disambiguationData":[TD([[makeQuery(id+"F0.imprint","IMPRINT",EDGE,{"derivedFrom":subQ0}),1.0]])]});}
            var Q3;
            {var subQ0=sQuery(id+"F0.wireOp",EDGE,"E45");var subQ1=sQuery(id+"F0.wireOp",EDGE,"E44");var subQ2=makeQuery(id+"F0.imprint","INTERSECT",VERTEX,{"disambiguationData":[OD(0.0)],"derivedFrom":[subQ1,subQ0]});Q3=makeQuery(id+"F0.imprint","IMPRINT",FACE,{"disambiguationData":[TD([[makeQuery(id+"F0.imprint","IMPRINT",EDGE,{"disambiguationData":[TD([[subQ2,1.0]])],"derivedFrom":subQ1}),-1.0]])]});}
            extrude(context, id + "F4", {"entities" : qUnion([Q0, Q1, Q2, Q3]), "depth" : 11.43 * mm});
        }
        {
            var Q0;
            {var subQ0=sQuery(id+"F0.wireOp",EDGE,"E28");Q0=makeQuery(id+"F0.imprint","IMPRINT",FACE,{"disambiguationData":[TD([[makeQuery(id+"F0.imprint","IMPRINT",EDGE,{"derivedFrom":subQ0}),-1.0]])]});}
            var Q1;
            {var subQ0=sQuery(id+"F0.wireOp",EDGE,"E19");Q1=makeQuery(id+"F0.imprint","IMPRINT",FACE,{"disambiguationData":[TD([[makeQuery(id+"F0.imprint","IMPRINT",EDGE,{"derivedFrom":subQ0}),-1.0]])]});}
            extrude(context, id + "F5", {"entities" : qUnion([Q0, Q1]), "operationType" : NewBodyOperationType.ADD, "depth" : 13.72 * mm});
        }
        {
            var Q0;
            {var subQ3=sQuery(id+"F0.wireOp",EDGE,"E68");Q0=makeQuery(id+"F0.imprint","IMPRINT",FACE,{"disambiguationData":[TD([[makeQuery(id+"F0.imprint","IMPRINT",EDGE,{"derivedFrom":subQ3}),1.0]])]});}
            extrude(context, id + "F6", {"entities" : qUnion([Q0]), "operationType" : NewBodyOperationType.ADD, "depth" : 8.13 * mm});
        }
        {
            var Q0;
            {var subQ4=sQuery(id+"F0.wireOp",EDGE,"E68");Q0=makeQuery(id+"F0.imprint","IMPRINT",FACE,{"disambiguationData":[TD([[makeQuery(id+"F0.imprint","IMPRINT",EDGE,{"derivedFrom":subQ4}),-1.0]])]});}
            var Q1;
            {var subQ0=sQuery(id+"F0.wireOp",EDGE,"E71");var subQ1=sQuery(id+"F0.wireOp",EDGE,"E69");var subQ2=makeQuery(id+"F0.imprint","INTERSECT",VERTEX,{"derivedFrom":[subQ1,subQ0]});Q1=makeQuery(id+"F0.imprint","IMPRINT",FACE,{"disambiguationData":[TD([[makeQuery(id+"F0.imprint","IMPRINT",EDGE,{"disambiguationData":[TD([[subQ2,1.0]])],"derivedFrom":subQ1}),1.0]])]});}
            var Q2;
            {var subQ3=sQuery(id+"F0.wireOp",EDGE,"E52");Q2=makeQuery(id+"F0.imprint","IMPRINT",FACE,{"disambiguationData":[TD([[makeQuery(id+"F0.imprint","IMPRINT",EDGE,{"derivedFrom":subQ3}),1.0]])]});}
            var Q3;
            Q3=makeQuery(id+"F0.imprint","IMPRINT",FACE,{"disambiguationData":[TD([[makeQuery(id+"F0.imprint","IMPRINT",EDGE,{"derivedFrom":sQuery(id+"F0.wireOp",EDGE,"E79")}),1.0]])]});
            var Q4;
            Q4=makeQuery(id+"F0.imprint","IMPRINT",FACE,{"disambiguationData":[TD([[makeQuery(id+"F0.imprint","IMPRINT",EDGE,{"derivedFrom":sQuery(id+"F0.wireOp",EDGE,"E78")}),1.0]])]});
            extrude(context, id + "F7", {"entities" : qUnion([Q0, Q1, Q2, Q3, Q4]), "operationType" : NewBodyOperationType.ADD, "depth" : 9.14 * mm});
        }
        {
            var Q0;
            {var subQ1=sQuery(id+"F0.wireOp",EDGE,"E46");var subQ5=makeQuery(id+"F0.imprint","INTERSECT",VERTEX,{"derivedFrom":[subQ1,sQuery(id+"F0.wireOp",EDGE,"E76")]});Q0=makeQuery(id+"F0.imprint","IMPRINT",FACE,{"disambiguationData":[TD([[makeQuery(id+"F0.imprint","IMPRINT",EDGE,{"disambiguationData":[TD([[subQ5,-1.0]])],"derivedFrom":subQ1}),-1.0]])]});}
            var Q1;
            {var subQ7=sQuery(id+"F0.wireOp",EDGE,"E70");Q1=makeQuery(id+"F0.imprint","IMPRINT",FACE,{"disambiguationData":[TD([[makeQuery(id+"F0.imprint","IMPRINT",EDGE,{"derivedFrom":subQ7}),1.0]])]});}
            extrude(context, id + "F8", {"entities" : qUnion([Q0, Q1]), "depth" : 10.16 * mm});
        }
        {
            var Q0;
            {var subQ3=sQuery(id+"F0.wireOp",EDGE,"E90");Q0=makeQuery(id+"F0.imprint","IMPRINT",FACE,{"disambiguationData":[TD([[makeQuery(id+"F0.imprint","IMPRINT",EDGE,{"derivedFrom":subQ3}),1.0]])]});}
            var Q1;
            {var subQ1=sQuery(id+"F0.wireOp",EDGE,"E52");Q1=makeQuery(id+"F0.imprint","IMPRINT",FACE,{"disambiguationData":[TD([[makeQuery(id+"F0.imprint","IMPRINT",EDGE,{"derivedFrom":subQ1}),-1.0]])]});}
            var Q2;
            {var subQ0=sQuery(id+"F0.wireOp",EDGE,"E87");Q2=makeQuery(id+"F0.imprint","IMPRINT",FACE,{"disambiguationData":[TD([[makeQuery(id+"F0.imprint","IMPRINT",EDGE,{"derivedFrom":subQ0}),-1.0]])]});}
            extrude(context, id + "F9", {"entities" : qUnion([Q0, Q1, Q2]), "depth" : 10.16 * mm});
        }
        {
            var Q0;
            {var subQ0=sQuery(id+"F0.wireOp",EDGE,"E92");Q0=makeQuery(id+"F0.imprint","IMPRINT",FACE,{"disambiguationData":[TD([[makeQuery(id+"F0.imprint","IMPRINT",EDGE,{"derivedFrom":subQ0}),1.0]])]});}
            var Q1;
            {var subQ0=sQuery(id+"F0.wireOp",EDGE,"E74");Q1=makeQuery(id+"F0.imprint","IMPRINT",FACE,{"disambiguationData":[TD([[makeQuery(id+"F0.imprint","IMPRINT",EDGE,{"derivedFrom":subQ0}),1.0]])]});}
            extrude(context, id + "F10", {"entities" : qUnion([Q0, Q1]), "depth" : 11.18 * mm});
        }
        {
            var Q0;
            {var subQ0=sQuery(id+"F0.wireOp",EDGE,"E93");Q0=makeQuery(id+"F0.imprint","IMPRINT",FACE,{"disambiguationData":[TD([[makeQuery(id+"F0.imprint","IMPRINT",EDGE,{"derivedFrom":subQ0}),-1.0]])]});}
            var Q1;
            {var subQ7=sQuery(id+"F0.wireOp",EDGE,"E55");var subQ10=sQuery(id+"F0.wireOp",EDGE,"E54");var subQ11=makeQuery(id+"F0.imprint","INTERSECT",VERTEX,{"derivedFrom":[subQ10,subQ7]});Q1=makeQuery(id+"F0.imprint","IMPRINT",FACE,{"disambiguationData":[TD([[makeQuery(id+"F0.imprint","IMPRINT",EDGE,{"disambiguationData":[TD([[subQ11,1.0]])],"derivedFrom":subQ10}),1.0]])]});}
            extrude(context, id + "F11", {"entities" : qUnion([Q0, Q1]), "depth" : 12.2 * mm});
        }
        {
            var Q0;
            {var subQ0=sQuery(id+"F0.wireOp",EDGE,"E58");Q0=makeQuery(id+"F0.imprint","IMPRINT",FACE,{"disambiguationData":[TD([[makeQuery(id+"F0.imprint","IMPRINT",EDGE,{"derivedFrom":subQ0}),-1.0]])]});}
            var Q1;
            {var subQ0=sQuery(id+"F0.wireOp",EDGE,"E60");Q1=makeQuery(id+"F0.imprint","IMPRINT",FACE,{"disambiguationData":[TD([[makeQuery(id+"F0.imprint","IMPRINT",EDGE,{"derivedFrom":subQ0}),1.0]])]});}
            var Q2;
            {var subQ0=sQuery(id+"F0.wireOp",EDGE,"E62");Q2=makeQuery(id+"F0.imprint","IMPRINT",FACE,{"disambiguationData":[TD([[makeQuery(id+"F0.imprint","IMPRINT",EDGE,{"derivedFrom":subQ0}),1.0]])]});}
            var Q3;
            {var subQ0=sQuery(id+"F0.wireOp",EDGE,"E95");Q3=makeQuery(id+"F0.imprint","IMPRINT",FACE,{"disambiguationData":[TD([[makeQuery(id+"F0.imprint","IMPRINT",EDGE,{"derivedFrom":subQ0}),-1.0]])]});}
            var Q4;
            {var subQ0=sQuery(id+"F0.wireOp",EDGE,"E97");Q4=makeQuery(id+"F0.imprint","IMPRINT",FACE,{"disambiguationData":[TD([[makeQuery(id+"F0.imprint","IMPRINT",EDGE,{"derivedFrom":subQ0}),-1.0]])]});}
            var Q5;
            {var subQ0=sQuery(id+"F0.wireOp",EDGE,"E99");Q5=makeQuery(id+"F0.imprint","IMPRINT",FACE,{"disambiguationData":[TD([[makeQuery(id+"F0.imprint","IMPRINT",EDGE,{"derivedFrom":subQ0}),-1.0]])]});}
            extrude(context, id + "F12", {"entities" : qUnion([Q0, Q1, Q2, Q3, Q4, Q5]), "depth" : 12.45 * mm});
        }
        {
            var Q0;
            {var subQ0=sQuery(id+"F0.wireOp",EDGE,"E62");Q0=makeQuery(id+"F0.imprint","IMPRINT",FACE,{"disambiguationData":[TD([[makeQuery(id+"F0.imprint","IMPRINT",EDGE,{"derivedFrom":subQ0}),-1.0]])]});}
            var Q1;
            {var subQ0=sQuery(id+"F0.wireOp",EDGE,"E67");var subQ1=makeQuery(id+"F0.imprint","INTERSECT",VERTEX,{"derivedFrom":[sQuery(id+"F0.wireOp",EDGE,"E64"),subQ0]});Q1=makeQuery(id+"F0.imprint","IMPRINT",FACE,{"disambiguationData":[TD([[makeQuery(id+"F0.imprint","IMPRINT",EDGE,{"disambiguationData":[TD([[subQ1,1.0]])],"derivedFrom":subQ0}),1.0]])]});}
            extrude(context, id + "F13", {"entities" : qUnion([Q0, Q1]), "depth" : 8.38 * mm});
        }
        {
            var Q0;
            {var subQ1=sQuery(id+"F0.wireOp",EDGE,"E76");Q0=makeQuery(id+"F0.imprint","IMPRINT",FACE,{"disambiguationData":[TD([[makeQuery(id+"F0.imprint","IMPRINT",EDGE,{"derivedFrom":subQ1}),1.0]])]});}
            var Q1;
            Q1=makeQuery(id+"F0.imprint","IMPRINT",FACE,{"disambiguationData":[TD([[makeQuery(id+"F0.imprint","IMPRINT",EDGE,{"derivedFrom":sQuery(id+"F0.wireOp",EDGE,"E80")}),-1.0]])]});
            var Q2;
            Q2=makeQuery(id+"F0.imprint","IMPRINT",FACE,{"disambiguationData":[TD([[makeQuery(id+"F0.imprint","IMPRINT",EDGE,{"derivedFrom":sQuery(id+"F0.wireOp",EDGE,"E84")}),1.0]])]});
            extrude(context, id + "F14", {"entities" : qUnion([Q0, Q1, Q2]), "depth" : 10.16 * mm});
        }
        {
            var Q0;
            {var subQ3=sQuery(id+"F0.wireOp",EDGE,"E101");Q0=makeQuery(id+"F0.imprint","IMPRINT",FACE,{"disambiguationData":[TD([[makeQuery(id+"F0.imprint","IMPRINT",EDGE,{"derivedFrom":subQ3}),1.0]])]});}
            extrude(context, id + "F15", {"entities" : qUnion([Q0]), "depth" : 10.03 * mm});
        }
        {
            var Q0;
            Q0=qCreatedBy(makeId("Front.planeOp"),FACE);
            var sketch = newSketch(context, id + "F16", { "sketchPlane" : qUnion([Q0])});
            skCircle(sketch, "E105", {"center": v(-7.76, 56.73) * mm, "radius": 2.52 * mm});
            skSolve(sketch);
        }
        {
            var Q0;
            Q0=sQuery(id+"F16.wireOp",VERTEX,"E105.center");
            var Q1;
            Q1=makeQuery(id+"F10.opExtrude","SWEPT_BODY",BODY,{"disambiguationData":[OSD([sQuery(id+"F0.wireOp",EDGE,"E69"),sQuery(id+"F0.wireOp",EDGE,"E73"),sQuery(id+"F0.wireOp",EDGE,"E74"),sQuery(id+"F0.wireOp",EDGE,"E75")])]});
            hole(context, id + "F17", {"style" : HoleStyle.SIMPLE, "endStyle" : HoleEndStyle.THROUGH, "oppositeDirection" : true, "holeDiameter" : 6.35 * mm, "isTappedThrough" : true, "tappedDepth" : 12.7 * mm, "tapClearance" : 3, "locations" : qUnion([Q0]), "scope" : qUnion([Q1])});
        }
    });
